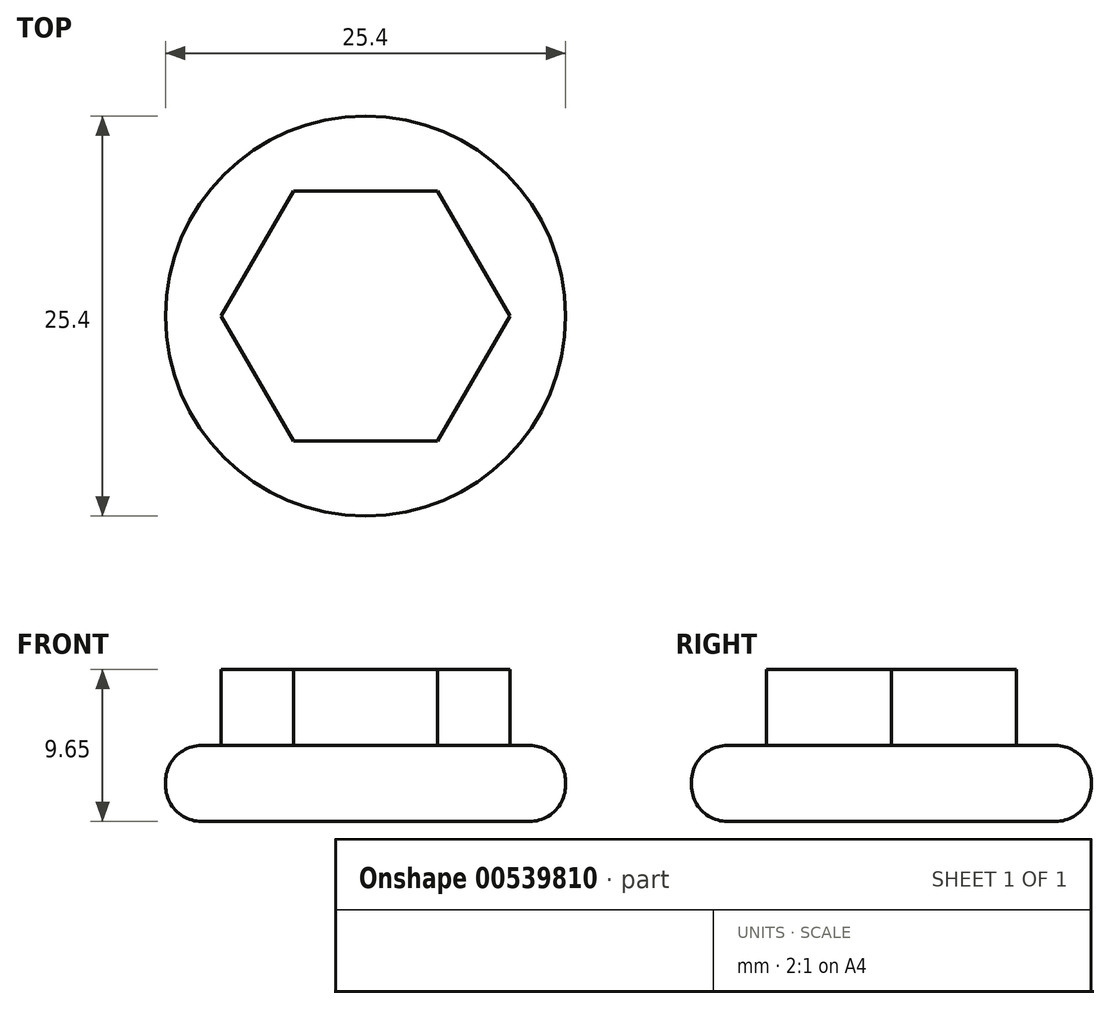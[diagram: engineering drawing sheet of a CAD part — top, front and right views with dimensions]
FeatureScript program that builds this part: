
annotation { "Feature Type Name" : "Feature", "Feature Type Description" : "" }
export const myFeature = defineFeature(function(context is Context, id is Id, definition is map)
    precondition{}
    {
        {
            var Q0;
            Q0=qCreatedBy(makeId("Top.planeOp"),FACE);
            var sketch = newSketch(context, id + "F0", { "sketchPlane" : qUnion([Q0])});
            skCircle(sketch, "E0", {"center": v(0, 0) * mm, "radius": 12.7 * mm});
            skSolve(sketch);
        }
        {
            var Q0;
            Q0 = qSketchRegion(id + "F0", true);
            extrude(context, id + "F1", {"entities" : qUnion([Q0]), "depth" : 4.83 * mm, "offsetDistance" : 25.4 * mm});
        }
        {
            var Q0;
            Q0=makeQuery(id+"F1.opExtrude","CAP_FACE",FACE,{"disambiguationData":[OSD([sQuery(id+"F0.wireOp",EDGE,"E0")])],"isStart":false});
            var sketch = newSketch(context, id + "F2", { "sketchPlane" : qUnion([Q0])});
            skCircle(sketch, "E1.cCircle", {"center": v(0, 0) * mm, "radius": 7.94 * mm, "construction": true});
            skLineSegment(sketch, "E1.0", {"start": v(-4.58, 7.94) * mm, "end": v(4.58, 7.94) * mm});
            skLineSegment(sketch, "E1.1", {"start": v(4.58, 7.94) * mm, "end": v(9.17, 0) * mm});
            skLineSegment(sketch, "E1.2", {"start": v(9.17, 0) * mm, "end": v(4.58, -7.94) * mm});
            skLineSegment(sketch, "E1.3", {"start": v(4.58, -7.94) * mm, "end": v(-4.58, -7.94) * mm});
            skLineSegment(sketch, "E1.4", {"start": v(-4.58, -7.94) * mm, "end": v(-9.17, 0) * mm});
            skLineSegment(sketch, "E1.5", {"start": v(-9.17, 0) * mm, "end": v(-4.58, 7.94) * mm});
            skPoint(sketch, "E1.0.midPoint", {"position": v(0, 7.94) * mm});
            skSolve(sketch);
        }
        {
            var Q0;
            Q0=makeQuery(id+"F2.imprint","IMPRINT",FACE,{"disambiguationData":[TD([[makeQuery(id+"F2.imprint","IMPRINT",EDGE,{"derivedFrom":sQuery(id+"F2.wireOp",EDGE,"E1.0")}),-1.0]])]});
            extrude(context, id + "F3", {"entities" : qUnion([Q0]), "operationType" : NewBodyOperationType.ADD, "depth" : 4.83 * mm, "offsetDistance" : 25.4 * mm});
        }
        {
            var Q0;
            Q0=makeQuery(id+"F1.opExtrude","CAP_EDGE",EDGE,{"disambiguationData":[OSD([sQuery(id+"F0.wireOp",EDGE,"E0")])],"isStart":false});
            fillet(context, id + "F4", {"entities" : qUnion([Q0]), "radius" : 2.3 * mm, "tangentPropagation" : true, "allowEdgeOverflow" : false});
        }
        {
            var Q0;
            Q0=makeQuery(id+"F1.opExtrude","CAP_EDGE",EDGE,{"disambiguationData":[OSD([sQuery(id+"F0.wireOp",EDGE,"E0")])],"isStart":true});
            fillet(context, id + "F5", {"entities" : qUnion([Q0]), "radius" : 2.3 * mm, "tangentPropagation" : true, "allowEdgeOverflow" : false});
        }
    });
